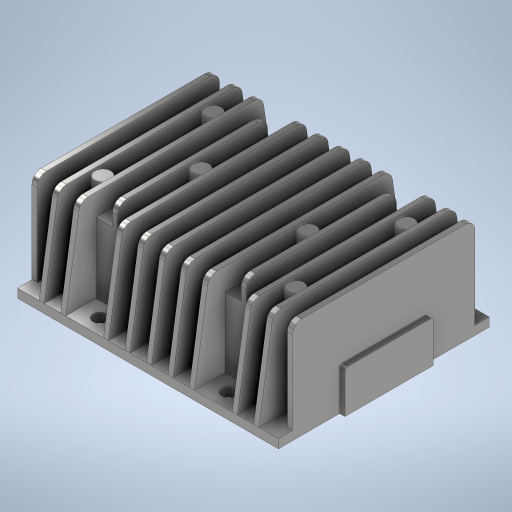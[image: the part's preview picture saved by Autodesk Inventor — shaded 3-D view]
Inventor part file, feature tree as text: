
AUTODESK INVENTOR PART (.ipt)
format: ipt  version: 2023 (Build 270158000, 158)  size: 636,416 bytes
history: native  units: in
note: dims shown in document units (in); Inventor stores cm internally (conversion verified against a paired STEP export)
features: extrude x17, sketch x16, plane x11, projected_geometry x5, fillet x1
ambient origin geometry x8: Origin, YZ Plane, XZ Plane, XY Plane, X Axis, Y Axis, Z Axis, Center Point
bodies: Solid1 (feature_tree)
feature tree (50):
  sketch  "Sketch2"  dims[d0=1.5098in d1=2.7244in]
  extrude  "Extrusion1"  Depth=2.7244in
  extrude  "Extrusion2"  Depth=0.1339in
  plane  "Work Plane1"
  extrude  "Extrusion3"  Depth=0.1378in
  plane  "Work Plane2"
  extrude  "Extrusion4"  Depth=1.1811in
  plane  "Work Plane3"
  extrude  "Extrusion5"  Depth=0.2421in
  plane  "Work Plane4"
  extrude  "Extrusion6"  Depth=0.1378in
  plane  "Work Plane5"
  extrude  "Extrusion7"  Depth=0.0787in TaperAngle=0.0deg
  plane  "Work Plane6"
  extrude  "Extrusion8"  Depth=0.1378in
  plane  "Work Plane7"
  extrude  "Extrusion9"  Depth=0.2421in
  plane  "Work Plane8"
  extrude  "Extrusion10"  Depth=0.2421in
  plane  "Work Plane9"
  extrude  "Extrusion11"  Depth=0.2421in
  plane  "Work Plane10"
  extrude  "Extrusion12"  Depth=0.2421in
  plane  "Work Plane11"
  extrude  "Extrusion13"  Depth=0.2421in
  extrude  "Extrusion14"  Depth=0.2421in
  extrude  "Extrusion15"  Depth=0.2421in
  extrude  "Extrusion16"  Depth=0.2421in
  extrude  "Extrusion17"  Depth=0.0787in TaperAngle=0.0deg
  fillet  "Fillet1"  Radius=0.0787in
  sketch  "Sketch3"  dims[d4=3.1496in d5=0.1339in]
  sketch  "Sketch4"  dims[d6=0.0787in d7=0.0in d8=0.1378in]
  sketch  "Sketch5"  dims[d9=0.2421in d10=1.1811in]
  sketch  "Sketch6"  dims[d11=3.8976in d12=0.0in d13=0.2421in]
  sketch  "Sketch7"  dims[d14=0.0787in d15=0.0in d16=0.1378in]
  sketch  "Sketch8"  dims[d17=0.2421in d18=0.0787in d19=0.0in]
  sketch  "Sketch9"  dims[d20=0.2421in d21=0.1378in]
  sketch  "Sketch10"  dims[d22=0.0787in d23=0.0in d24=0.2421in]
  sketch  "Sketch11"  dims[d25=0.0787in d26=0.0in d27=0.2421in]
  projected_geometry  "Projected Loop1"
  sketch  "Sketch12"  dims[d28=0.0787in d29=0.0in d30=0.2421in]
  projected_geometry  "Projected Loop2"
  sketch  "Sketch13"  dims[d31=0.0787in d32=0.0in d33=0.2421in]
  projected_geometry  "Projected Loop3"
  sketch  "Sketch14"  dims[d34=0.0787in d35=0.0in d36=0.2421in]
  projected_geometry  "Projected Loop4"
  sketch  "Sketch15"  dims[d37=0.0787in d38=0.0in d39=0.2421in]
  projected_geometry  "Projected Loop5"
  sketch  "Sketch16"  dims[d40=0.0787in d41=0.0in d42=0.2421in]
  sketch  "Sketch17"  dims[d43=0.0787in d44=0.0in d45=0.2421in d46=0.0787in d47=0.0in d48=0.0787in d49=0.0in d50=0.2047in d51=0.2047in d52=0.2047in d53=0.2047in d54=0.0394in d55=0.0394in d56=0.0394in d57=0.0394in d58=0.4547in d59=0.2274in d60=0.2274in d61=0.2274in d62=0.2274in d63=0.0in d64=0.0in d65=0.2421in d66=0.2421in d67=0.2421in d68=0.2421in d69=0.2421in d70=0.2421in d71=2.2402in d72=1.1201in d73=1.1201in d74=0.1211in d75=0.1211in d76=0.1211in d77=0.1211in d78=0.1211in d79=0.1211in d80=0.2953in d81=0.2953in d82=0.2953in d83=0.2953in d84=0.2953in d85=0.0in d86=0.6299in d87=1.3189in d88=0.7028in d89=2.7244in d90=0.0787in d91=0.0in d92=0.0394in]
